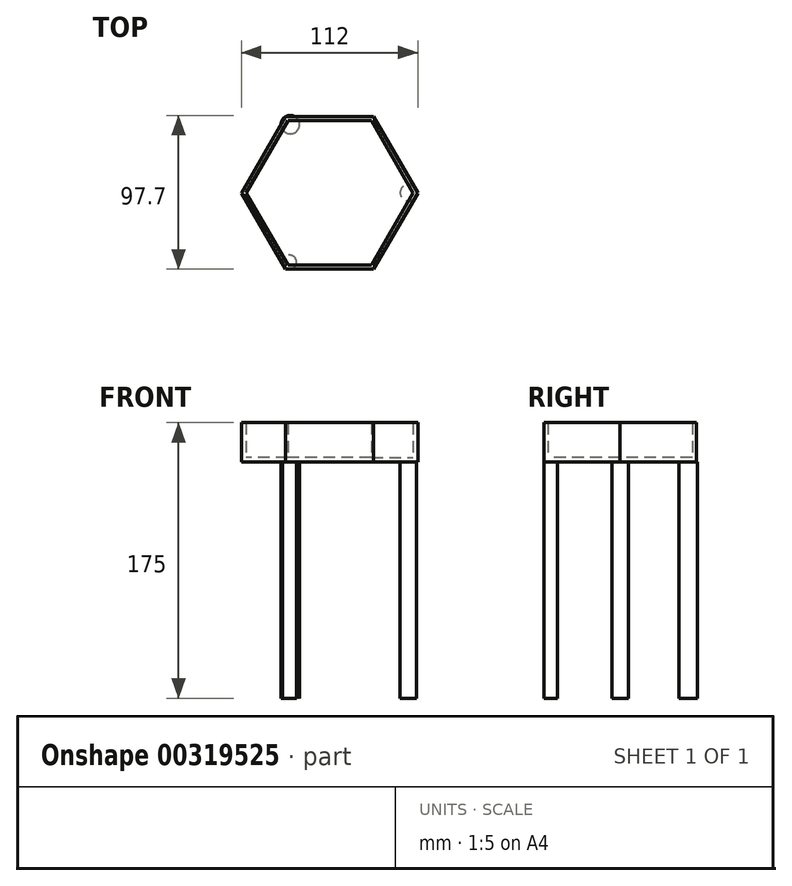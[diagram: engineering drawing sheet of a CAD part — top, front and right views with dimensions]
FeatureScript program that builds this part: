
annotation { "Feature Type Name" : "Feature", "Feature Type Description" : "" }
export const myFeature = defineFeature(function(context is Context, id is Id, definition is map)
    precondition{}
    {
        {
            var Q0;
            Q0=qCreatedBy(makeId("Top.planeOp"),FACE);
            var sketch = newSketch(context, id + "F0", { "sketchPlane" : qUnion([Q0])});
            skCircle(sketch, "E0.cCircle", {"center": v(0, 0) * mm, "radius": 56 * mm, "construction": true});
            skLineSegment(sketch, "E0.0", {"start": v(56, 0) * mm, "end": v(28, -48.5) * mm});
            skLineSegment(sketch, "E0.1", {"start": v(28, -48.5) * mm, "end": v(-28, -48.5) * mm});
            skLineSegment(sketch, "E0.2", {"start": v(-28, -48.5) * mm, "end": v(-56, 0) * mm});
            skLineSegment(sketch, "E0.3", {"start": v(-56, 0) * mm, "end": v(-28, 48.5) * mm});
            skLineSegment(sketch, "E0.4", {"start": v(-28, 48.5) * mm, "end": v(28, 48.5) * mm});
            skLineSegment(sketch, "E0.5", {"start": v(28, 48.5) * mm, "end": v(56, 0) * mm});
            skCircle(sketch, "E1.cCircle", {"center": v(0, 0) * mm, "radius": 53 * mm, "construction": true});
            skLineSegment(sketch, "E1.0", {"start": v(53, 0) * mm, "end": v(26.5, -45.9) * mm});
            skLineSegment(sketch, "E1.1", {"start": v(26.5, -45.9) * mm, "end": v(-26.5, -45.9) * mm});
            skLineSegment(sketch, "E1.2", {"start": v(-26.5, -45.9) * mm, "end": v(-53, 0) * mm});
            skLineSegment(sketch, "E1.3", {"start": v(-53, 0) * mm, "end": v(-26.5, 45.9) * mm});
            skLineSegment(sketch, "E1.4", {"start": v(-26.5, 45.9) * mm, "end": v(26.5, 45.9) * mm});
            skLineSegment(sketch, "E1.5", {"start": v(26.5, 45.9) * mm, "end": v(53, 0) * mm});
            skSolve(sketch);
        }
        {
            var Q0;
            Q0=makeQuery(id+"F0.imprint","IMPRINT",FACE,{"disambiguationData":[TD([[makeQuery(id+"F0.imprint","IMPRINT",EDGE,{"derivedFrom":sQuery(id+"F0.wireOp",EDGE,"E0.0")}),-1.0]])]});
            extrude(context, id + "F1", {"entities" : qUnion([Q0]), "depth" : 25 * mm});
        }
        {
            var Q0;
            Q0=makeQuery(id+"F0.imprint","IMPRINT",FACE,{"disambiguationData":[TD([[makeQuery(id+"F0.imprint","IMPRINT",EDGE,{"derivedFrom":sQuery(id+"F0.wireOp",EDGE,"E1.0")}),-1.0]])]});
            extrude(context, id + "F2", {"entities" : qUnion([Q0]), "operationType" : NewBodyOperationType.ADD, "depth" : 3 * mm});
        }
        {
            var Q0;
            Q0=qCreatedBy(makeId("Top.planeOp"),FACE);
            var sketch = newSketch(context, id + "F3", { "sketchPlane" : qUnion([Q0])});
            skCircle(sketch, "E2", {"center": v(-25.37, -44.03) * mm, "radius": 4.39 * mm});
            skCircle(sketch, "E3", {"center": v(-24.97, 43.32) * mm, "radius": 5.89 * mm});
            skCircle(sketch, "E4", {"center": v(50, 0) * mm, "radius": 5.19 * mm});
            skSolve(sketch);
        }
        {
            var Q0;
            Q0=makeQuery(id+"F3.imprint","IMPRINT",FACE,{"disambiguationData":[TD([[makeQuery(id+"F3.imprint","IMPRINT",EDGE,{"derivedFrom":sQuery(id+"F3.wireOp",EDGE,"E2")}),1.0]])]});
            extrude(context, id + "F4", {"entities" : qUnion([Q0]), "operationType" : NewBodyOperationType.ADD, "oppositeDirection" : true, "depth" : 150 * mm});
        }
        {
            var Q0;
            Q0=makeQuery(id+"F3.imprint","IMPRINT",FACE,{"disambiguationData":[TD([[makeQuery(id+"F3.imprint","IMPRINT",EDGE,{"derivedFrom":sQuery(id+"F3.wireOp",EDGE,"E4")}),1.0]])]});
            extrude(context, id + "F5", {"entities" : qUnion([Q0]), "operationType" : NewBodyOperationType.ADD, "oppositeDirection" : true, "depth" : 150 * mm});
        }
        {
            var Q0;
            Q0=makeQuery(id+"F3.imprint","IMPRINT",FACE,{"disambiguationData":[TD([[makeQuery(id+"F3.imprint","IMPRINT",EDGE,{"derivedFrom":sQuery(id+"F3.wireOp",EDGE,"E2")}),1.0]])]});
            var Q1;
            Q1=makeQuery(id+"F3.imprint","IMPRINT",FACE,{"disambiguationData":[TD([[makeQuery(id+"F3.imprint","IMPRINT",EDGE,{"derivedFrom":sQuery(id+"F3.wireOp",EDGE,"E4")}),1.0]])]});
            var Q2;
            Q2=makeQuery(id+"F3.imprint","IMPRINT",FACE,{"disambiguationData":[TD([[makeQuery(id+"F3.imprint","IMPRINT",EDGE,{"derivedFrom":sQuery(id+"F3.wireOp",EDGE,"E3")}),1.0]])]});
            extrude(context, id + "F6", {"entities" : qUnion([Q0, Q1, Q2]), "operationType" : NewBodyOperationType.ADD, "oppositeDirection" : true, "depth" : 150 * mm});
        }
    });
